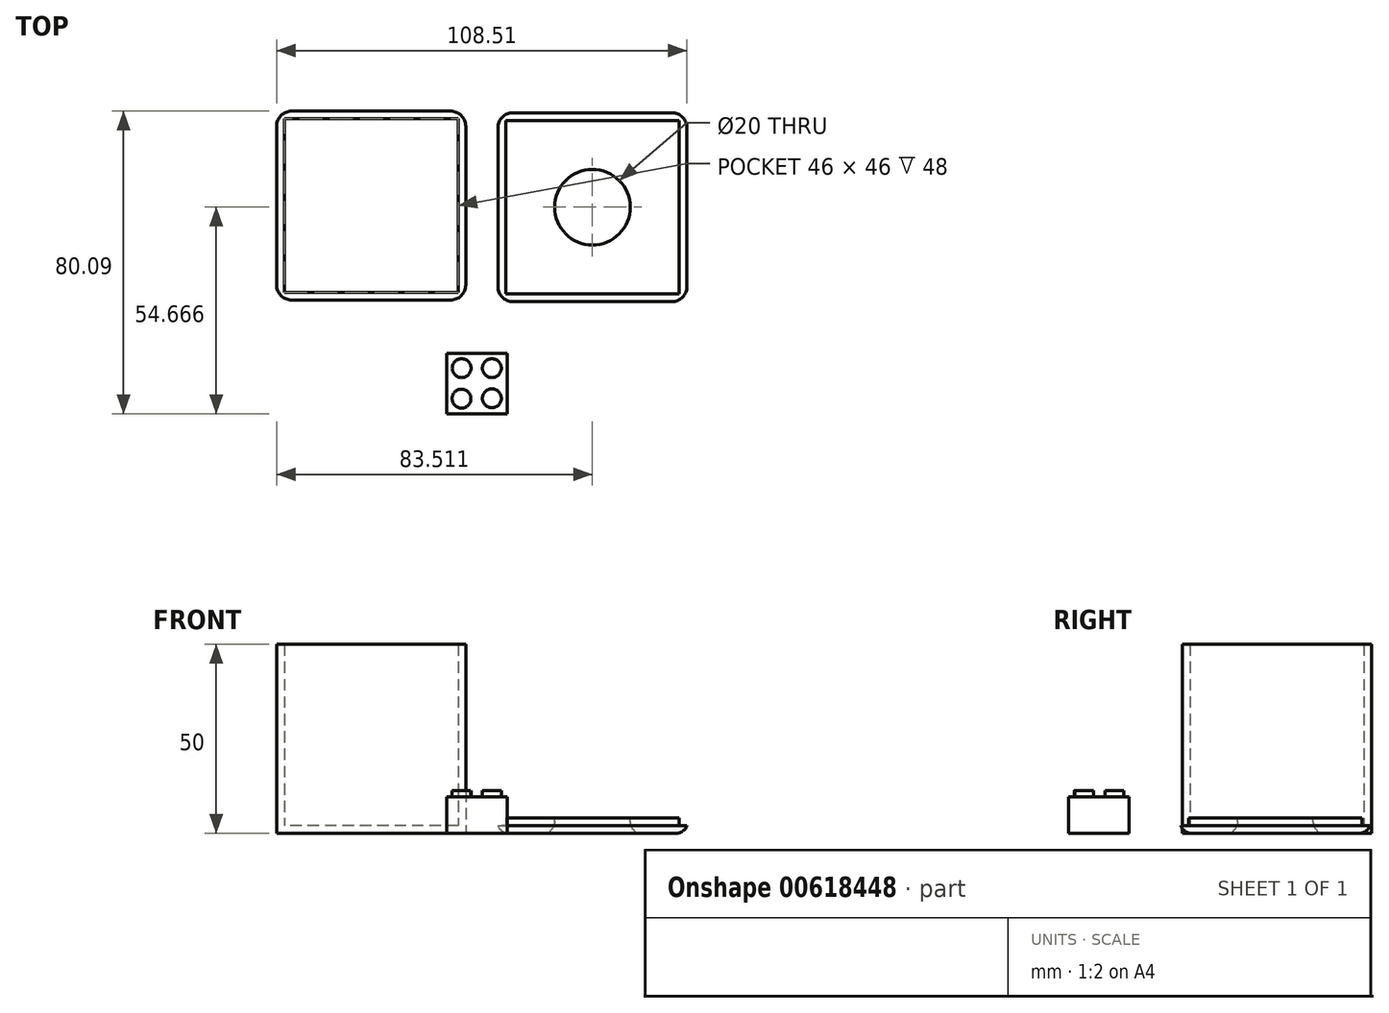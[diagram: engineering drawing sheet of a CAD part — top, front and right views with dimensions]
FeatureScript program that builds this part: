
annotation { "Feature Type Name" : "Feature", "Feature Type Description" : "" }
export const myFeature = defineFeature(function(context is Context, id is Id, definition is map)
    precondition{}
    {
        {
            var Q0;
            Q0=qCreatedBy(makeId("Top.planeOp"),FACE);
            var sketch = newSketch(context, id + "F0", { "sketchPlane" : qUnion([Q0])});
            skLineSegment(sketch, "E0.bottom", {"start": v(-23.33, -14.27) * mm, "end": v(-73.33, -14.27) * mm});
            skLineSegment(sketch, "E0.top", {"start": v(-23.33, 35.73) * mm, "end": v(-73.33, 35.73) * mm});
            skLineSegment(sketch, "E0.left", {"start": v(-23.33, -14.27) * mm, "end": v(-23.33, 35.73) * mm});
            skLineSegment(sketch, "E0.right", {"start": v(-73.33, -14.27) * mm, "end": v(-73.33, 35.73) * mm});
            skPoint(sketch, "E0.middle", {"position": v(-48.33, 10.73) * mm});
            skLineSegment(sketch, "E1.0", {"start": v(-71.33, -12.27) * mm, "end": v(-71.33, 33.73) * mm});
            skLineSegment(sketch, "E1.1", {"start": v(-25.33, -12.27) * mm, "end": v(-71.33, -12.27) * mm});
            skLineSegment(sketch, "E1.2", {"start": v(-25.33, -12.27) * mm, "end": v(-25.33, 33.73) * mm});
            skLineSegment(sketch, "E1.3", {"start": v(-25.33, 33.73) * mm, "end": v(-71.33, 33.73) * mm});
            skSolve(sketch);
        }
        {
            var Q0;
            Q0=makeQuery(id+"F0.imprint","IMPRINT",FACE,{"disambiguationData":[TD([[makeQuery(id+"F0.imprint","IMPRINT",EDGE,{"derivedFrom":sQuery(id+"F0.wireOp",EDGE,"E1.0")}),-1.0]])]});
            extrude(context, id + "F1", {"entities" : qUnion([Q0]), "depth" : 2 * mm, "offsetDistance" : 25 * mm});
        }
        {
            var Q0;
            Q0 = qSketchRegion(id + "F0", true);
            extrude(context, id + "F2", {"entities" : qUnion([Q0]), "operationType" : NewBodyOperationType.ADD, "depth" : 50 * mm, "offsetDistance" : 25 * mm});
        }
        {
            var Q0;
            Q0=qCreatedBy(makeId("Top.planeOp"),FACE);
            var sketch = newSketch(context, id + "F3", { "sketchPlane" : qUnion([Q0])});
            skLineSegment(sketch, "E2.bottom", {"start": v(65.08, -17.8) * mm, "end": v(15.08, -17.8) * mm});
            skLineSegment(sketch, "E2.top", {"start": v(65.08, 32.2) * mm, "end": v(15.08, 32.2) * mm});
            skLineSegment(sketch, "E2.left", {"start": v(65.08, -17.8) * mm, "end": v(65.08, 32.2) * mm});
            skLineSegment(sketch, "E2.right", {"start": v(15.08, -17.8) * mm, "end": v(15.08, 32.2) * mm});
            skPoint(sketch, "E2.middle", {"position": v(40.08, 7.2) * mm});
            skLineSegment(sketch, "E3.0", {"start": v(62.98, -15.7) * mm, "end": v(17.18, -15.7) * mm});
            skLineSegment(sketch, "E3.1", {"start": v(62.98, -15.7) * mm, "end": v(62.98, 30.1) * mm});
            skLineSegment(sketch, "E3.2", {"start": v(62.98, 30.1) * mm, "end": v(17.18, 30.1) * mm});
            skLineSegment(sketch, "E3.3", {"start": v(17.18, -15.7) * mm, "end": v(17.18, 30.1) * mm});
            skSolve(sketch);
        }
        {
            var Q0;
            Q0=makeQuery(id+"F3.imprint","IMPRINT",FACE,{"disambiguationData":[TD([[makeQuery(id+"F3.imprint","IMPRINT",EDGE,{"derivedFrom":sQuery(id+"F3.wireOp",EDGE,"E3.0")}),-1.0]])]});
            extrude(context, id + "F4", {"entities" : qUnion([Q0]), "depth" : 4 * mm, "offsetDistance" : 25 * mm});
        }
        {
            var Q0;
            Q0 = qSketchRegion(id + "F3", true);
            extrude(context, id + "F5", {"entities" : qUnion([Q0]), "operationType" : NewBodyOperationType.ADD, "depth" : 2 * mm, "offsetDistance" : 25 * mm});
        }
        {
            var Q0;
            Q0=makeQuery(id+"F4.opExtrude","CAP_FACE",FACE,{"disambiguationData":[OSD([sQuery(id+"F3.wireOp",EDGE,"E3.0"),sQuery(id+"F3.wireOp",EDGE,"E3.1"),sQuery(id+"F3.wireOp",EDGE,"E3.2"),sQuery(id+"F3.wireOp",EDGE,"E3.3")])],"isStart":false});
            var sketch = newSketch(context, id + "F6", { "sketchPlane" : qUnion([Q0])});
            skCircle(sketch, "E4", {"center": v(40.08, 7.2) * mm, "radius": 10 * mm});
            skPoint(sketch, "E4.centerSnap0", {"position": v(40.08, -15.7) * mm});
            skPoint(sketch, "E4.centerSnap1", {"position": v(62.98, 7.2) * mm});
            skSolve(sketch);
        }
        {
            var Q0;
            Q0 = qSketchRegion(id + "F6", true);
            extrude(context, id + "F7", {"entities" : qUnion([Q0]), "operationType" : NewBodyOperationType.REMOVE, "oppositeDirection" : true, "depth" : 10 * mm, "offsetDistance" : 25 * mm});
        }
        {
            var Q0;
            Q0=makeQuery(id+"F4.opExtrude","SWEPT_BODY",BODY,{"disambiguationData":[OSD([sQuery(id+"F3.wireOp",EDGE,"E3.0"),sQuery(id+"F3.wireOp",EDGE,"E3.1"),sQuery(id+"F3.wireOp",EDGE,"E3.2"),sQuery(id+"F3.wireOp",EDGE,"E3.3")])]});
            transform(context, id + "F8", {"entities" : qUnion([Q0]), "transformType" : TransformType.TRANSLATION_3D, "dx" : 0 * mm, "dy" : 3.1 * mm, "dz" : 0 * mm, "makeCopy" : false});
        }
        {
            var Q0;
            Q0=makeQuery(id+"F1.opExtrude","SWEPT_BODY",BODY,{"disambiguationData":[OSD([sQuery(id+"F0.wireOp",EDGE,"E1.0"),sQuery(id+"F0.wireOp",EDGE,"E1.1"),sQuery(id+"F0.wireOp",EDGE,"E1.2"),sQuery(id+"F0.wireOp",EDGE,"E1.3")])]});
            transform(context, id + "F9", {"entities" : qUnion([Q0]), "transformType" : TransformType.TRANSLATION_3D, "dx" : 20.4 * mm, "dy" : 0 * mm, "dz" : 0 * mm, "makeCopy" : false});
        }
        {
            var Q0;
            Q0=makeQuery(id+"F4.opExtrude","SWEPT_BODY",BODY,{"disambiguationData":[OSD([sQuery(id+"F3.wireOp",EDGE,"E3.0"),sQuery(id+"F3.wireOp",EDGE,"E3.1"),sQuery(id+"F3.wireOp",EDGE,"E3.2"),sQuery(id+"F3.wireOp",EDGE,"E3.3")])]});
            transform(context, id + "F10", {"entities" : qUnion([Q0]), "transformType" : TransformType.TRANSLATION_3D, "dx" : -9.5 * mm, "dy" : 0 * mm, "dz" : 0 * mm, "makeCopy" : false});
        }
        {
            var Q0;
            Q0=makeQuery(id+"F2.opExtrude","SWEPT_EDGE",EDGE,{"disambiguationData":[OSD([sQuery(id+"F0.wireOp",EDGE,"E0.bottom"),sQuery(id+"F0.wireOp",EDGE,"E0.left")])]});
            var Q1;
            Q1=makeQuery(id+"F2.opExtrude","SWEPT_EDGE",EDGE,{"disambiguationData":[OSD([sQuery(id+"F0.wireOp",EDGE,"E0.top"),sQuery(id+"F0.wireOp",EDGE,"E0.left")])]});
            var Q2;
            Q2=makeQuery(id+"F2.opExtrude","SWEPT_EDGE",EDGE,{"disambiguationData":[OSD([sQuery(id+"F0.wireOp",EDGE,"E0.top"),sQuery(id+"F0.wireOp",EDGE,"E0.right")])]});
            var Q3;
            Q3=makeQuery(id+"F2.opExtrude","SWEPT_EDGE",EDGE,{"disambiguationData":[OSD([sQuery(id+"F0.wireOp",EDGE,"E0.bottom"),sQuery(id+"F0.wireOp",EDGE,"E0.right")])]});
            var Q4;
            Q4=makeQuery(id+"F5.opExtrude","SWEPT_EDGE",EDGE,{"disambiguationData":[OSD([sQuery(id+"F3.wireOp",EDGE,"E2.top"),sQuery(id+"F3.wireOp",EDGE,"E2.right")])]});
            var Q5;
            Q5=makeQuery(id+"F5.opExtrude","SWEPT_EDGE",EDGE,{"disambiguationData":[OSD([sQuery(id+"F3.wireOp",EDGE,"E2.top"),sQuery(id+"F3.wireOp",EDGE,"E2.left")])]});
            var Q6;
            Q6=makeQuery(id+"F5.opExtrude","SWEPT_EDGE",EDGE,{"disambiguationData":[OSD([sQuery(id+"F3.wireOp",EDGE,"E2.bottom"),sQuery(id+"F3.wireOp",EDGE,"E2.left")])]});
            var Q7;
            Q7=makeQuery(id+"F5.opExtrude","SWEPT_EDGE",EDGE,{"disambiguationData":[OSD([sQuery(id+"F3.wireOp",EDGE,"E2.bottom"),sQuery(id+"F3.wireOp",EDGE,"E2.right")])]});
            fillet(context, id + "F11", {"entities" : qUnion([Q0, Q1, Q2, Q3, Q4, Q5, Q6, Q7]), "radius" : 4 * mm, "tangentPropagation" : true, "allowEdgeOverflow" : false});
        }
        {
            var Q0;
            {var subQ0=sQuery(id+"F3.wireOp",EDGE,"E3.3");var subQ1=sQuery(id+"F3.wireOp",EDGE,"E3.2");var subQ2=sQuery(id+"F3.wireOp",EDGE,"E3.1");var subQ3=sQuery(id+"F3.wireOp",EDGE,"E3.0");Q0=makeQuery(id+"F5.boolean.opBoolean","MERGE",FACE,{"derivedFrom":[makeQuery(id+"F4.opExtrude","CAP_FACE",FACE,{"disambiguationData":[OSD([subQ3,subQ2,subQ1,subQ0])],"isStart":true}),makeQuery(id+"F5.opExtrude","CAP_FACE",FACE,{"disambiguationData":[OSD([sQuery(id+"F3.wireOp",EDGE,"E2.bottom"),sQuery(id+"F3.wireOp",EDGE,"E2.top"),sQuery(id+"F3.wireOp",EDGE,"E2.left"),sQuery(id+"F3.wireOp",EDGE,"E2.right"),subQ3,subQ2,subQ1,subQ0])],"isStart":true})]});}
            fillet(context, id + "F12", {"entities" : qUnion([Q0]), "radius" : 3 * mm, "tangentPropagation" : true, "allowEdgeOverflow" : false});
        }
        {
            var Q0;
            Q0=qCreatedBy(makeId("Top.planeOp"),FACE);
            var sketch = newSketch(context, id + "F13", { "sketchPlane" : qUnion([Q0])});
            skLineSegment(sketch, "E5.bottom", {"start": v(8, -44.36) * mm, "end": v(-8, -44.36) * mm});
            skLineSegment(sketch, "E5.top", {"start": v(8, -28.36) * mm, "end": v(-8, -28.36) * mm});
            skLineSegment(sketch, "E5.left", {"start": v(8, -44.36) * mm, "end": v(8, -28.36) * mm});
            skLineSegment(sketch, "E5.right", {"start": v(-8, -44.36) * mm, "end": v(-8, -28.36) * mm});
            skPoint(sketch, "E5.middle", {"position": v(0, -36.36) * mm});
            skPoint(sketch, "E6", {"position": v(-4.42, -39.87) * mm});
            skPoint(sketch, "E7", {"position": v(3.58, -39.87) * mm});
            skPoint(sketch, "E8", {"position": v(3.58, -31.87) * mm});
            skPoint(sketch, "E9", {"position": v(-4.42, -31.87) * mm});
            skSolve(sketch);
        }
        {
            var Q0;
            Q0=makeQuery(id+"F13.imprint","IMPRINT",FACE,{"disambiguationData":[TD([[makeQuery(id+"F13.imprint","IMPRINT",EDGE,{"derivedFrom":sQuery(id+"F13.wireOp",EDGE,"E5.bottom")}),-1.0]])]});
            extrude(context, id + "F14", {"entities" : qUnion([Q0]), "depth" : 9.6 * mm, "offsetDistance" : 25 * mm});
        }
        {
            var Q0;
            Q0=makeQuery(id+"F14.opExtrude","CAP_FACE",FACE,{"disambiguationData":[OSD([sQuery(id+"F13.wireOp",EDGE,"E5.bottom"),sQuery(id+"F13.wireOp",EDGE,"E5.top"),sQuery(id+"F13.wireOp",EDGE,"E5.left"),sQuery(id+"F13.wireOp",EDGE,"E5.right")])],"isStart":false});
            var sketch = newSketch(context, id + "F15", { "sketchPlane" : qUnion([Q0])});
            skPoint(sketch, "E10", {"position": v(-4, -32.36) * mm});
            skPoint(sketch, "E11", {"position": v(4, -32.36) * mm});
            skPoint(sketch, "E12", {"position": v(4, -40.36) * mm});
            skPoint(sketch, "E13", {"position": v(-4, -40.36) * mm});
            skLineSegment(sketch, "E14", {"start": v(-8, -36.36) * mm, "end": v(8, -36.36) * mm, "construction": true});
            skLineSegment(sketch, "E15", {"start": v(8, -36.36) * mm, "end": v(0, -28.36) * mm, "construction": true});
            skLineSegment(sketch, "E16", {"start": v(0, -28.36) * mm, "end": v(-8, -36.36) * mm, "construction": true});
            skLineSegment(sketch, "E17", {"start": v(-8, -36.36) * mm, "end": v(0, -44.36) * mm, "construction": true});
            skLineSegment(sketch, "E18", {"start": v(0, -44.36) * mm, "end": v(8, -36.36) * mm, "construction": true});
            skSolve(sketch);
        }
        {
            var Q0;
            Q0=makeQuery(id+"F15.imprint","IMPRINT",FACE,{"disambiguationData":[TD([[makeQuery(id+"F15.imprint","IMPRINT",EDGE,{"derivedFrom":makeQuery(id+"F14.opExtrude","CAP_EDGE",EDGE,{"disambiguationData":[OSD([sQuery(id+"F13.wireOp",EDGE,"E5.bottom")])],"isStart":false})}),-1.0]])]});
            var sketch = newSketch(context, id + "F16", { "sketchPlane" : qUnion([Q0])});
            skCircle(sketch, "E19", {"center": v(-4, -32.3) * mm, "radius": 2.5 * mm});
            skCircle(sketch, "E20", {"center": v(4, -32.3) * mm, "radius": 2.5 * mm});
            skCircle(sketch, "E21", {"center": v(-4.04, -40.36) * mm, "radius": 2.5 * mm});
            skCircle(sketch, "E22", {"center": v(4, -40.27) * mm, "radius": 2.5 * mm});
            skSolve(sketch);
        }
        {
            var Q0;
            Q0 = qSketchRegion(id + "F16", true);
            extrude(context, id + "F17", {"entities" : qUnion([Q0]), "operationType" : NewBodyOperationType.ADD, "depth" : 1.7 * mm, "offsetDistance" : 25 * mm});
        }
    });
